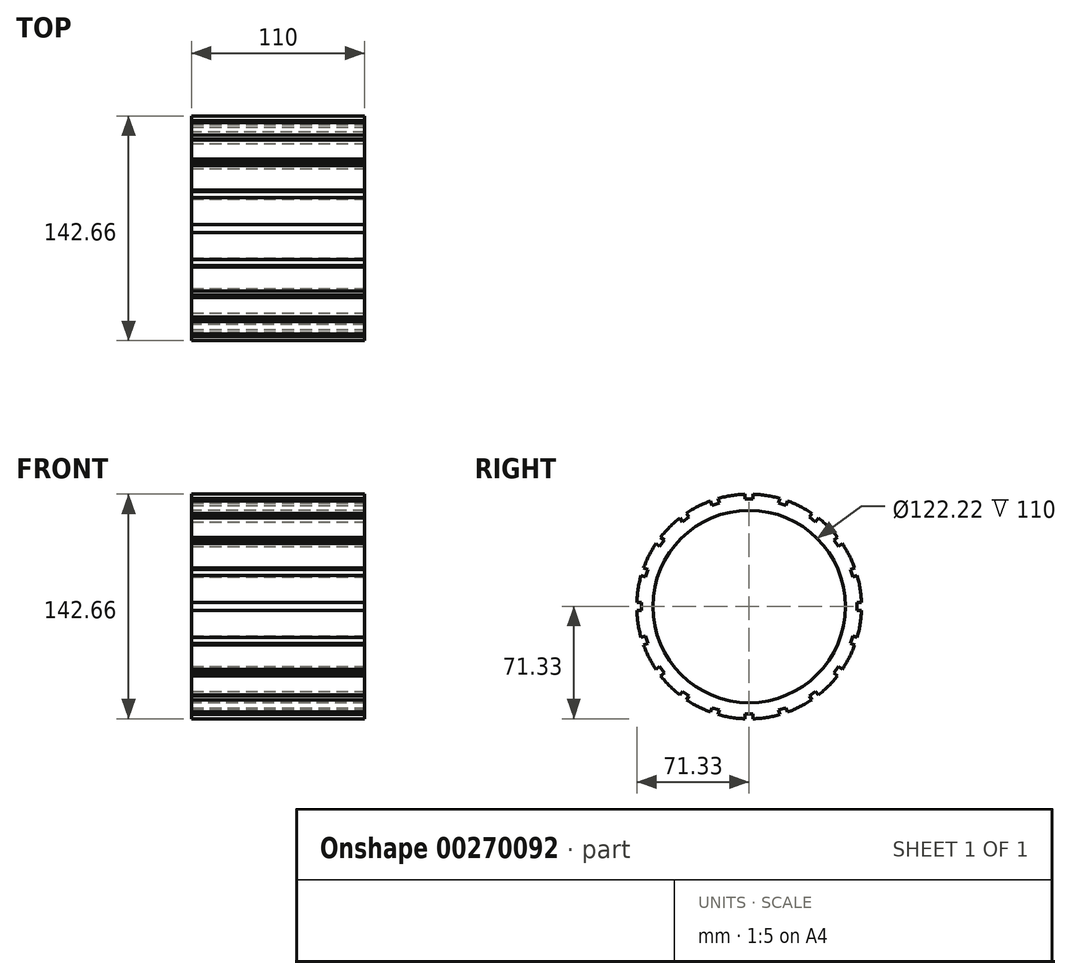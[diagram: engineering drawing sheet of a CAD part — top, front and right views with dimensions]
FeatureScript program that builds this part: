
annotation { "Feature Type Name" : "Feature", "Feature Type Description" : "" }
export const myFeature = defineFeature(function(context is Context, id is Id, definition is map)
    precondition{}
    {
        {
            var Q0;
            Q0=qCreatedBy(makeId("Top.planeOp"),FACE);
            var sketch = newSketch(context, id + "F0", { "sketchPlane" : qUnion([Q0])});
            skLineSegment(sketch, "E0.bottom", {"start": v(-55, 71.37) * mm, "end": v(55, 71.37) * mm});
            skPoint(sketch, "E1", {"position": v(0, 71.37) * mm});
            skLineSegment(sketch, "E2", {"start": v(-55, 61.1) * mm, "end": v(55, 61.1) * mm});
            skLineSegment(sketch, "E3", {"start": v(-55, 71.37) * mm, "end": v(-55, 61.1) * mm});
            skLineSegment(sketch, "E4", {"start": v(55, 71.37) * mm, "end": v(55, 61.1) * mm});
            skLineSegment(sketch, "E5", {"start": v(0, 0) * mm, "end": v(65.82, 0) * mm, "construction": true});
            skSolve(sketch);
        }
        {
            var Q0;
            Q0=makeQuery(id+"F0.imprint","IMPRINT",FACE,{"disambiguationData":[TD([[makeQuery(id+"F0.imprint","IMPRINT",EDGE,{"derivedFrom":sQuery(id+"F0.wireOp",EDGE,"E0.bottom")}),-1.0]])]});
            var Q1;
            Q1=sQuery(id+"F0.wireOp",EDGE,"E5");
            revolve(context, id + "F1", {"entities" : qUnion([Q0]), "axis" : qUnion([Q1]), "revolveType" : RevolveType.FULL});
        }
        {
            var Q0;
            Q0=makeQuery(id+"F1.opRevolve","SWEPT_FACE",FACE,{"disambiguationData":[OSD([sQuery(id+"F0.wireOp",EDGE,"E4")])]});
            var sketch = newSketch(context, id + "F2", { "sketchPlane" : qUnion([Q0])});
            skPoint(sketch, "E6.center", {"position": v(0, 0) * mm});
            skLineSegment(sketch, "E7", {"start": v(0, 91.35) * mm, "end": v(0, -13.72) * mm, "construction": true});
            skLineSegment(sketch, "E8.bottom", {"start": v(-2.5, 71.37) * mm, "end": v(2.5, 71.37) * mm});
            skLineSegment(sketch, "E8.top", {"start": v(-2.5, 68.37) * mm, "end": v(2.5, 68.37) * mm});
            skLineSegment(sketch, "E8.left", {"start": v(-2.5, 71.37) * mm, "end": v(-2.5, 68.37) * mm});
            skLineSegment(sketch, "E8.right", {"start": v(2.5, 71.37) * mm, "end": v(2.5, 68.37) * mm});
            skPoint(sketch, "E9", {"position": v(0, 71.37) * mm});
            skPoint(sketch, "E10", {"position": v(0, 68.37) * mm});
            skLineSegment(sketch, "E11.1.0", {"start": v(-19.68, 68.65) * mm, "end": v(-18.75, 65.8) * mm});
            skLineSegment(sketch, "E11.1.1", {"start": v(-24.43, 67.1) * mm, "end": v(-19.68, 68.65) * mm});
            skLineSegment(sketch, "E11.1.2", {"start": v(-24.43, 67.1) * mm, "end": v(-23.5, 64.25) * mm});
            skLineSegment(sketch, "E11.1.3", {"start": v(-23.5, 64.25) * mm, "end": v(-18.75, 65.8) * mm});
            skLineSegment(sketch, "E11.2.0", {"start": v(-39.93, 59.21) * mm, "end": v(-38.17, 56.79) * mm});
            skLineSegment(sketch, "E11.2.1", {"start": v(-43.98, 56.27) * mm, "end": v(-39.93, 59.21) * mm});
            skLineSegment(sketch, "E11.2.2", {"start": v(-43.98, 56.27) * mm, "end": v(-42.21, 53.85) * mm});
            skLineSegment(sketch, "E11.2.3", {"start": v(-42.21, 53.85) * mm, "end": v(-38.17, 56.79) * mm});
            skLineSegment(sketch, "E11.3.0", {"start": v(-56.27, 43.98) * mm, "end": v(-53.85, 42.21) * mm});
            skLineSegment(sketch, "E11.3.1", {"start": v(-59.21, 39.93) * mm, "end": v(-56.27, 43.98) * mm});
            skLineSegment(sketch, "E11.3.2", {"start": v(-59.21, 39.93) * mm, "end": v(-56.79, 38.17) * mm});
            skLineSegment(sketch, "E11.3.3", {"start": v(-56.79, 38.17) * mm, "end": v(-53.85, 42.21) * mm});
            skLineSegment(sketch, "E11.4.0", {"start": v(-67.1, 24.43) * mm, "end": v(-64.25, 23.5) * mm});
            skLineSegment(sketch, "E11.4.1", {"start": v(-68.65, 19.68) * mm, "end": v(-67.1, 24.43) * mm});
            skLineSegment(sketch, "E11.4.2", {"start": v(-68.65, 19.68) * mm, "end": v(-65.8, 18.75) * mm});
            skLineSegment(sketch, "E11.4.3", {"start": v(-65.8, 18.75) * mm, "end": v(-64.25, 23.5) * mm});
            skLineSegment(sketch, "E11.5.0", {"start": v(-71.37, 2.5) * mm, "end": v(-68.37, 2.5) * mm});
            skLineSegment(sketch, "E11.5.1", {"start": v(-71.37, -2.5) * mm, "end": v(-71.37, 2.5) * mm});
            skLineSegment(sketch, "E11.5.2", {"start": v(-71.37, -2.5) * mm, "end": v(-68.37, -2.5) * mm});
            skLineSegment(sketch, "E11.5.3", {"start": v(-68.37, -2.5) * mm, "end": v(-68.37, 2.5) * mm});
            skLineSegment(sketch, "E11.6.0", {"start": v(-68.65, -19.68) * mm, "end": v(-65.8, -18.75) * mm});
            skLineSegment(sketch, "E11.6.1", {"start": v(-67.1, -24.43) * mm, "end": v(-68.65, -19.68) * mm});
            skLineSegment(sketch, "E11.6.2", {"start": v(-67.1, -24.43) * mm, "end": v(-64.25, -23.5) * mm});
            skLineSegment(sketch, "E11.6.3", {"start": v(-64.25, -23.5) * mm, "end": v(-65.8, -18.75) * mm});
            skLineSegment(sketch, "E11.7.0", {"start": v(-59.21, -39.93) * mm, "end": v(-56.79, -38.17) * mm});
            skLineSegment(sketch, "E11.7.1", {"start": v(-56.27, -43.98) * mm, "end": v(-59.21, -39.93) * mm});
            skLineSegment(sketch, "E11.7.2", {"start": v(-56.27, -43.98) * mm, "end": v(-53.85, -42.21) * mm});
            skLineSegment(sketch, "E11.7.3", {"start": v(-53.85, -42.21) * mm, "end": v(-56.79, -38.17) * mm});
            skLineSegment(sketch, "E11.8.0", {"start": v(-43.98, -56.27) * mm, "end": v(-42.21, -53.85) * mm});
            skLineSegment(sketch, "E11.8.1", {"start": v(-39.93, -59.21) * mm, "end": v(-43.98, -56.27) * mm});
            skLineSegment(sketch, "E11.8.2", {"start": v(-39.93, -59.21) * mm, "end": v(-38.17, -56.79) * mm});
            skLineSegment(sketch, "E11.8.3", {"start": v(-38.17, -56.79) * mm, "end": v(-42.21, -53.85) * mm});
            skLineSegment(sketch, "E11.9.0", {"start": v(-24.43, -67.1) * mm, "end": v(-23.5, -64.25) * mm});
            skLineSegment(sketch, "E11.9.1", {"start": v(-19.68, -68.65) * mm, "end": v(-24.43, -67.1) * mm});
            skLineSegment(sketch, "E11.9.2", {"start": v(-19.68, -68.65) * mm, "end": v(-18.75, -65.8) * mm});
            skLineSegment(sketch, "E11.9.3", {"start": v(-18.75, -65.8) * mm, "end": v(-23.5, -64.25) * mm});
            skLineSegment(sketch, "E11.10.0", {"start": v(-2.5, -71.37) * mm, "end": v(-2.5, -68.37) * mm});
            skLineSegment(sketch, "E11.10.1", {"start": v(2.5, -71.37) * mm, "end": v(-2.5, -71.37) * mm});
            skLineSegment(sketch, "E11.10.2", {"start": v(2.5, -71.37) * mm, "end": v(2.5, -68.37) * mm});
            skLineSegment(sketch, "E11.10.3", {"start": v(2.5, -68.37) * mm, "end": v(-2.5, -68.37) * mm});
            skLineSegment(sketch, "E11.11.0", {"start": v(19.68, -68.65) * mm, "end": v(18.75, -65.8) * mm});
            skLineSegment(sketch, "E11.11.1", {"start": v(24.43, -67.1) * mm, "end": v(19.68, -68.65) * mm});
            skLineSegment(sketch, "E11.11.2", {"start": v(24.43, -67.1) * mm, "end": v(23.5, -64.25) * mm});
            skLineSegment(sketch, "E11.11.3", {"start": v(23.5, -64.25) * mm, "end": v(18.75, -65.8) * mm});
            skLineSegment(sketch, "E11.12.0", {"start": v(39.93, -59.21) * mm, "end": v(38.17, -56.79) * mm});
            skLineSegment(sketch, "E11.12.1", {"start": v(43.98, -56.27) * mm, "end": v(39.93, -59.21) * mm});
            skLineSegment(sketch, "E11.12.2", {"start": v(43.98, -56.27) * mm, "end": v(42.21, -53.85) * mm});
            skLineSegment(sketch, "E11.12.3", {"start": v(42.21, -53.85) * mm, "end": v(38.17, -56.79) * mm});
            skLineSegment(sketch, "E11.13.0", {"start": v(56.27, -43.98) * mm, "end": v(53.85, -42.21) * mm});
            skLineSegment(sketch, "E11.13.1", {"start": v(59.21, -39.93) * mm, "end": v(56.27, -43.98) * mm});
            skLineSegment(sketch, "E11.13.2", {"start": v(59.21, -39.93) * mm, "end": v(56.79, -38.17) * mm});
            skLineSegment(sketch, "E11.13.3", {"start": v(56.79, -38.17) * mm, "end": v(53.85, -42.21) * mm});
            skLineSegment(sketch, "E11.14.0", {"start": v(67.1, -24.43) * mm, "end": v(64.25, -23.5) * mm});
            skLineSegment(sketch, "E11.14.1", {"start": v(68.65, -19.68) * mm, "end": v(67.1, -24.43) * mm});
            skLineSegment(sketch, "E11.14.2", {"start": v(68.65, -19.68) * mm, "end": v(65.8, -18.75) * mm});
            skLineSegment(sketch, "E11.14.3", {"start": v(65.8, -18.75) * mm, "end": v(64.25, -23.5) * mm});
            skLineSegment(sketch, "E11.15.0", {"start": v(71.37, -2.5) * mm, "end": v(68.37, -2.5) * mm});
            skLineSegment(sketch, "E11.15.1", {"start": v(71.37, 2.5) * mm, "end": v(71.37, -2.5) * mm});
            skLineSegment(sketch, "E11.15.2", {"start": v(71.37, 2.5) * mm, "end": v(68.37, 2.5) * mm});
            skLineSegment(sketch, "E11.15.3", {"start": v(68.37, 2.5) * mm, "end": v(68.37, -2.5) * mm});
            skLineSegment(sketch, "E11.16.0", {"start": v(68.65, 19.68) * mm, "end": v(65.8, 18.75) * mm});
            skLineSegment(sketch, "E11.16.1", {"start": v(67.1, 24.43) * mm, "end": v(68.65, 19.68) * mm});
            skLineSegment(sketch, "E11.16.2", {"start": v(67.1, 24.43) * mm, "end": v(64.25, 23.5) * mm});
            skLineSegment(sketch, "E11.16.3", {"start": v(64.25, 23.5) * mm, "end": v(65.8, 18.75) * mm});
            skLineSegment(sketch, "E11.17.0", {"start": v(59.21, 39.93) * mm, "end": v(56.79, 38.17) * mm});
            skLineSegment(sketch, "E11.17.1", {"start": v(56.27, 43.98) * mm, "end": v(59.21, 39.93) * mm});
            skLineSegment(sketch, "E11.17.2", {"start": v(56.27, 43.98) * mm, "end": v(53.85, 42.21) * mm});
            skLineSegment(sketch, "E11.17.3", {"start": v(53.85, 42.21) * mm, "end": v(56.79, 38.17) * mm});
            skLineSegment(sketch, "E11.18.0", {"start": v(43.98, 56.27) * mm, "end": v(42.21, 53.85) * mm});
            skLineSegment(sketch, "E11.18.1", {"start": v(39.93, 59.21) * mm, "end": v(43.98, 56.27) * mm});
            skLineSegment(sketch, "E11.18.2", {"start": v(39.93, 59.21) * mm, "end": v(38.17, 56.79) * mm});
            skLineSegment(sketch, "E11.18.3", {"start": v(38.17, 56.79) * mm, "end": v(42.21, 53.85) * mm});
            skLineSegment(sketch, "E11.19.0", {"start": v(24.43, 67.1) * mm, "end": v(23.5, 64.25) * mm});
            skLineSegment(sketch, "E11.19.1", {"start": v(19.68, 68.65) * mm, "end": v(24.43, 67.1) * mm});
            skLineSegment(sketch, "E11.19.2", {"start": v(19.68, 68.65) * mm, "end": v(18.75, 65.8) * mm});
            skLineSegment(sketch, "E11.19.3", {"start": v(18.75, 65.8) * mm, "end": v(23.5, 64.25) * mm});
            skSolve(sketch);
        }
        {
            var Q0;
            {var subQ5=sQuery(id+"F2.wireOp",EDGE,"E8.top");Q0=makeQuery(id+"F2.imprint","IMPRINT",FACE,{"disambiguationData":[TD([[makeQuery(id+"F2.imprint","IMPRINT",EDGE,{"derivedFrom":subQ5}),1.0]])]});}
            var Q1;
            {var subQ4=sQuery(id+"F2.wireOp",EDGE,"E11.19.3");Q1=makeQuery(id+"F2.imprint","IMPRINT",FACE,{"disambiguationData":[TD([[makeQuery(id+"F2.imprint","IMPRINT",EDGE,{"derivedFrom":subQ4}),1.0]])]});}
            var Q2;
            {var subQ4=sQuery(id+"F2.wireOp",EDGE,"E11.18.3");Q2=makeQuery(id+"F2.imprint","IMPRINT",FACE,{"disambiguationData":[TD([[makeQuery(id+"F2.imprint","IMPRINT",EDGE,{"derivedFrom":subQ4}),1.0]])]});}
            var Q3;
            {var subQ4=sQuery(id+"F2.wireOp",EDGE,"E11.17.3");Q3=makeQuery(id+"F2.imprint","IMPRINT",FACE,{"disambiguationData":[TD([[makeQuery(id+"F2.imprint","IMPRINT",EDGE,{"derivedFrom":subQ4}),1.0]])]});}
            var Q4;
            {var subQ4=sQuery(id+"F2.wireOp",EDGE,"E11.16.3");Q4=makeQuery(id+"F2.imprint","IMPRINT",FACE,{"disambiguationData":[TD([[makeQuery(id+"F2.imprint","IMPRINT",EDGE,{"derivedFrom":subQ4}),1.0]])]});}
            var Q5;
            {var subQ6=sQuery(id+"F2.wireOp",EDGE,"E11.15.3");Q5=makeQuery(id+"F2.imprint","IMPRINT",FACE,{"disambiguationData":[TD([[makeQuery(id+"F2.imprint","IMPRINT",EDGE,{"derivedFrom":subQ6}),1.0]])]});}
            var Q6;
            {var subQ4=sQuery(id+"F2.wireOp",EDGE,"E11.14.3");Q6=makeQuery(id+"F2.imprint","IMPRINT",FACE,{"disambiguationData":[TD([[makeQuery(id+"F2.imprint","IMPRINT",EDGE,{"derivedFrom":subQ4}),1.0]])]});}
            var Q7;
            {var subQ4=sQuery(id+"F2.wireOp",EDGE,"E11.13.3");Q7=makeQuery(id+"F2.imprint","IMPRINT",FACE,{"disambiguationData":[TD([[makeQuery(id+"F2.imprint","IMPRINT",EDGE,{"derivedFrom":subQ4}),1.0]])]});}
            var Q8;
            {var subQ0=sQuery(id+"F2.wireOp",EDGE,"E11.12.3");Q8=makeQuery(id+"F2.imprint","IMPRINT",FACE,{"disambiguationData":[TD([[makeQuery(id+"F2.imprint","IMPRINT",EDGE,{"derivedFrom":subQ0}),1.0]])]});}
            var Q9;
            {var subQ4=sQuery(id+"F2.wireOp",EDGE,"E11.11.3");Q9=makeQuery(id+"F2.imprint","IMPRINT",FACE,{"disambiguationData":[TD([[makeQuery(id+"F2.imprint","IMPRINT",EDGE,{"derivedFrom":subQ4}),1.0]])]});}
            var Q10;
            {var subQ4=sQuery(id+"F2.wireOp",EDGE,"E11.10.3");Q10=makeQuery(id+"F2.imprint","IMPRINT",FACE,{"disambiguationData":[TD([[makeQuery(id+"F2.imprint","IMPRINT",EDGE,{"derivedFrom":subQ4}),1.0]])]});}
            var Q11;
            {var subQ4=sQuery(id+"F2.wireOp",EDGE,"E11.9.3");Q11=makeQuery(id+"F2.imprint","IMPRINT",FACE,{"disambiguationData":[TD([[makeQuery(id+"F2.imprint","IMPRINT",EDGE,{"derivedFrom":subQ4}),1.0]])]});}
            var Q12;
            {var subQ4=sQuery(id+"F2.wireOp",EDGE,"E11.8.3");Q12=makeQuery(id+"F2.imprint","IMPRINT",FACE,{"disambiguationData":[TD([[makeQuery(id+"F2.imprint","IMPRINT",EDGE,{"derivedFrom":subQ4}),1.0]])]});}
            var Q13;
            {var subQ4=sQuery(id+"F2.wireOp",EDGE,"E11.7.3");Q13=makeQuery(id+"F2.imprint","IMPRINT",FACE,{"disambiguationData":[TD([[makeQuery(id+"F2.imprint","IMPRINT",EDGE,{"derivedFrom":subQ4}),1.0]])]});}
            var Q14;
            {var subQ4=sQuery(id+"F2.wireOp",EDGE,"E11.6.3");Q14=makeQuery(id+"F2.imprint","IMPRINT",FACE,{"disambiguationData":[TD([[makeQuery(id+"F2.imprint","IMPRINT",EDGE,{"derivedFrom":subQ4}),1.0]])]});}
            var Q15;
            {var subQ4=sQuery(id+"F2.wireOp",EDGE,"E11.5.3");Q15=makeQuery(id+"F2.imprint","IMPRINT",FACE,{"disambiguationData":[TD([[makeQuery(id+"F2.imprint","IMPRINT",EDGE,{"derivedFrom":subQ4}),1.0]])]});}
            var Q16;
            {var subQ0=sQuery(id+"F2.wireOp",EDGE,"E11.4.3");Q16=makeQuery(id+"F2.imprint","IMPRINT",FACE,{"disambiguationData":[TD([[makeQuery(id+"F2.imprint","IMPRINT",EDGE,{"derivedFrom":subQ0}),1.0]])]});}
            var Q17;
            {var subQ0=sQuery(id+"F2.wireOp",EDGE,"E11.3.3");Q17=makeQuery(id+"F2.imprint","IMPRINT",FACE,{"disambiguationData":[TD([[makeQuery(id+"F2.imprint","IMPRINT",EDGE,{"derivedFrom":subQ0}),1.0]])]});}
            var Q18;
            {var subQ6=sQuery(id+"F2.wireOp",EDGE,"E11.2.3");Q18=makeQuery(id+"F2.imprint","IMPRINT",FACE,{"disambiguationData":[TD([[makeQuery(id+"F2.imprint","IMPRINT",EDGE,{"derivedFrom":subQ6}),1.0]])]});}
            var Q19;
            {var subQ4=sQuery(id+"F2.wireOp",EDGE,"E11.1.3");Q19=makeQuery(id+"F2.imprint","IMPRINT",FACE,{"disambiguationData":[TD([[makeQuery(id+"F2.imprint","IMPRINT",EDGE,{"derivedFrom":subQ4}),1.0]])]});}
            var Q20;
            Q20=makeQuery(id+"F1.opRevolve","SWEPT_FACE",FACE,{"disambiguationData":[OSD([sQuery(id+"F0.wireOp",EDGE,"E3")])]});
            extrude(context, id + "F3", {"entities" : qUnion([Q0, Q1, Q2, Q3, Q4, Q5, Q6, Q7, Q8, Q9, Q10, Q11, Q12, Q13, Q14, Q15, Q16, Q17, Q18, Q19]), "operationType" : NewBodyOperationType.REMOVE, "endBound" : BoundingType.UP_TO_SURFACE, "oppositeDirection" : true, "endBoundEntityFace" : qUnion([Q20]), "depth" : 25 * mm});
        }
    });
